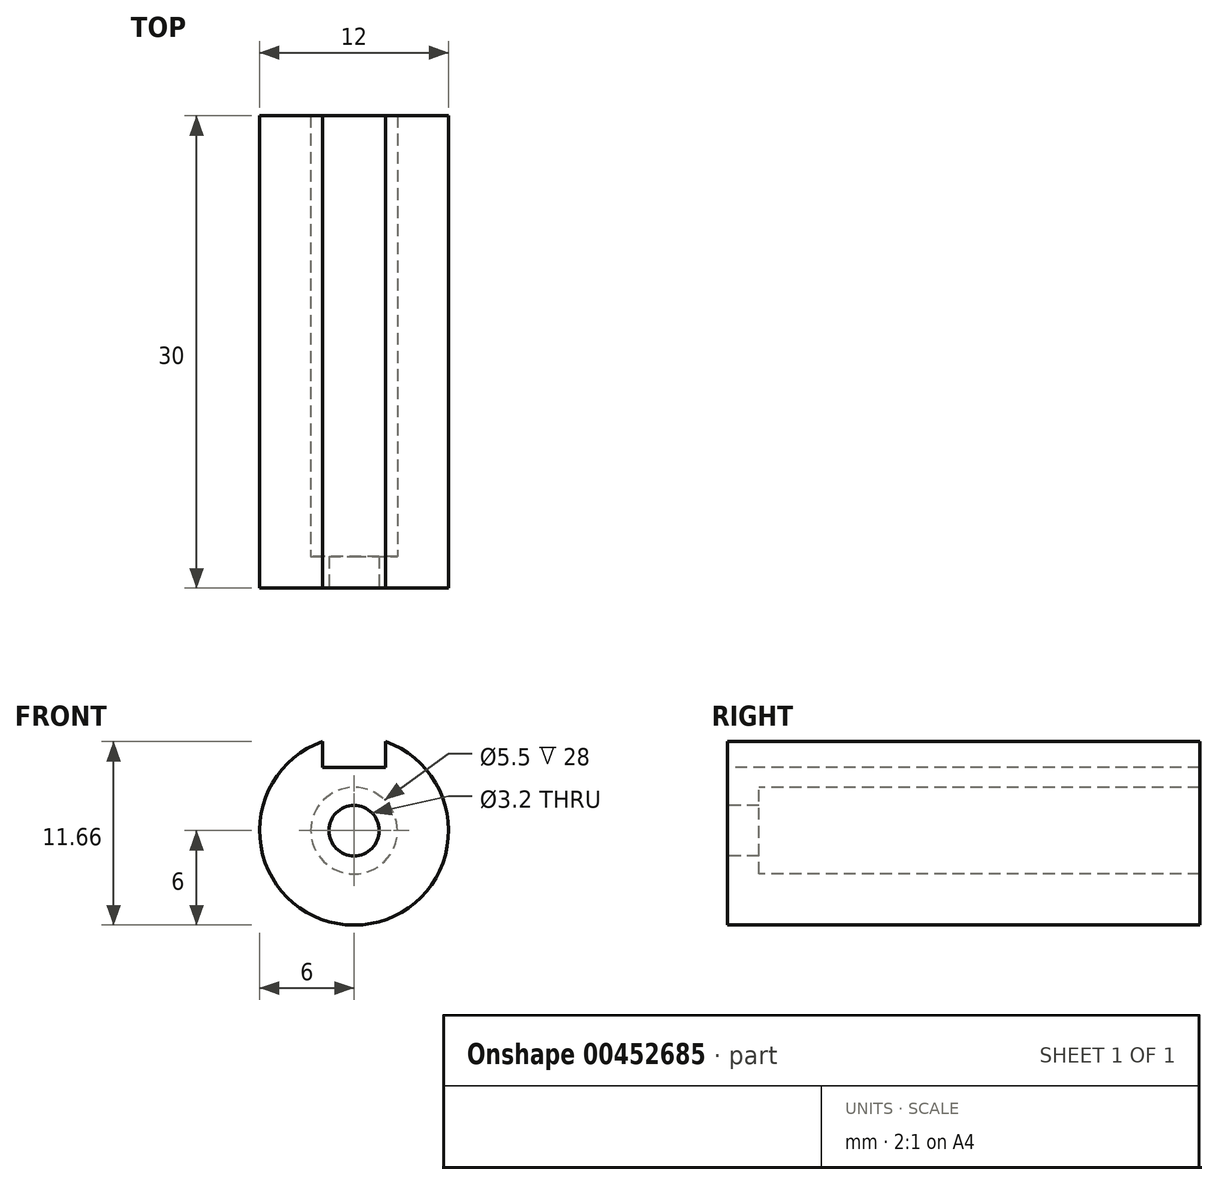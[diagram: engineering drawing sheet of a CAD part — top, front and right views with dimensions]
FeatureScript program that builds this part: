
annotation { "Feature Type Name" : "Feature", "Feature Type Description" : "" }
export const myFeature = defineFeature(function(context is Context, id is Id, definition is map)
    precondition{}
    {
        {
            var Q0;
            Q0=qCreatedBy(makeId("Front.planeOp"),FACE);
            var sketch = newSketch(context, id + "F0", { "sketchPlane" : qUnion([Q0])});
            skCircle(sketch, "E0", {"center": v(0, 0) * mm, "radius": 6 * mm});
            skSolve(sketch);
        }
        {
            var Q0;
            Q0=makeQuery(id+"F0.imprint","IMPRINT",FACE,{"disambiguationData":[TD([[makeQuery(id+"F0.imprint","IMPRINT",EDGE,{"derivedFrom":sQuery(id+"F0.wireOp",EDGE,"E0")}),1.0]])]});
            extrude(context, id + "F1", {"entities" : qUnion([Q0]), "depth" : 30 * mm});
        }
        {
            var Q0;
            Q0=makeQuery(id+"F1.opExtrude","CAP_FACE",FACE,{"disambiguationData":[OSD([sQuery(id+"F0.wireOp",EDGE,"E0")])],"isStart":false});
            var sketch = newSketch(context, id + "F2", { "sketchPlane" : qUnion([Q0])});
            skCircle(sketch, "E1", {"center": v(0, 0) * mm, "radius": 2.75 * mm});
            skSolve(sketch);
        }
        {
            var Q0;
            Q0=qSketchRegion(id+"F2",true);
            extrude(context, id + "F3", {"entities" : qUnion([Q0]), "operationType" : NewBodyOperationType.REMOVE, "endBound" : BoundingType.THROUGH_ALL, "oppositeDirection" : true, "depth" : 25 * mm});
        }
        {
            var Q0;
            Q0=qCreatedBy(makeId("Top.planeOp"),FACE);
            cPlane(context, id + "F4", {"entities" : qUnion([Q0]), "cplaneType" : CPlaneType.OFFSET, "offset" : 4 * mm, "width" : 150 * mm, "height" : 150 * mm});
        }
        {
            var Q0;
            Q0=qCreatedBy(id+"F4.planeOp",FACE);
            var Q1;
            Q1=makeQuery(id+"F1.opExtrude","CAP_EDGE",EDGE,{"disambiguationData":[OSD([sQuery(id+"F0.wireOp",EDGE,"E0")])],"isStart":false});
            cPlane(context, id + "F5", {"entities" : qUnion([Q0, Q1]), "cplaneType" : CPlaneType.LINE_ANGLE, "offset" : 25 * mm, "angle" : 45 * degree, "width" : 150 * mm, "height" : 150 * mm});
        }
        {
            var Q0;
            Q0=qCreatedBy(id+"F5.planeOp",FACE);
            cPlane(context, id + "F6", {"entities" : qUnion([Q0]), "cplaneType" : CPlaneType.OFFSET, "offset" : 3.5 * mm, "width" : 150 * mm, "height" : 150 * mm});
        }
        {
            var Q0;
            Q0=qCreatedBy(id+"F5.planeOp",FACE);
            var Q1;
            Q1=makeQuery(id+"F1.opExtrude","CAP_EDGE",EDGE,{"disambiguationData":[OSD([sQuery(id+"F0.wireOp",EDGE,"E0")])],"isStart":false});
            cPlane(context, id + "F7", {"entities" : qUnion([Q0, Q1]), "cplaneType" : CPlaneType.LINE_ANGLE, "offset" : 25 * mm, "angle" : 90 * degree, "width" : 150 * mm, "height" : 150 * mm});
        }
        {
            var Q0;
            Q0=makeQuery(id+"F1.opExtrude","CAP_FACE",FACE,{"disambiguationData":[OSD([sQuery(id+"F0.wireOp",EDGE,"E0")])],"isStart":false});
            var sketch = newSketch(context, id + "F8", { "sketchPlane" : qUnion([Q0])});
            skCircle(sketch, "E2", {"center": v(0, 0) * mm, "radius": 1.6 * mm});
            skCircle(sketch, "E3", {"center": v(0, 0) * mm, "radius": 5 * mm});
            skSolve(sketch);
        }
        {
            var Q0;
            Q0=qSketchRegion(id+"F8",true);
            extrude(context, id + "F9", {"entities" : qUnion([Q0]), "operationType" : NewBodyOperationType.ADD, "oppositeDirection" : true, "depth" : 2 * mm});
        }
        {
            var Q0;
            Q0=qCreatedBy(makeId("Right.planeOp"),FACE);
            cPlane(context, id + "F10", {"entities" : qUnion([Q0]), "cplaneType" : CPlaneType.OFFSET, "offset" : 6 * mm, "oppositeDirection" : true, "width" : 150 * mm, "height" : 150 * mm});
        }
        {
            var Q0;
            Q0=qCreatedBy(id+"F10.planeOp",FACE);
            var sketch = newSketch(context, id + "F11", { "sketchPlane" : qUnion([Q0])});
            skLineSegment(sketch, "E4.bottom", {"start": v(0, 2) * mm, "end": v(-30, 2) * mm});
            skLineSegment(sketch, "E4.top", {"start": v(0, -2) * mm, "end": v(-30, -2) * mm});
            skLineSegment(sketch, "E4.left", {"start": v(0, 2) * mm, "end": v(0, -2) * mm});
            skLineSegment(sketch, "E4.right", {"start": v(-30, 2) * mm, "end": v(-30, -2) * mm});
            skLineSegment(sketch, "E5", {"start": v(0, 0) * mm, "end": v(-30, 0) * mm, "construction": true});
            skPoint(sketch, "E5.startSnap0", {"position": v(0, 0) * mm});
            skSolve(sketch);
        }
        {
            var Q0;
            Q0=qCreatedBy(id+"F4.planeOp",FACE);
            var sketch = newSketch(context, id + "F12", { "sketchPlane" : qUnion([Q0])});
            skLineSegment(sketch, "E6.bottom", {"start": v(-2, 0) * mm, "end": v(2, 0) * mm});
            skLineSegment(sketch, "E6.top", {"start": v(-2, -30) * mm, "end": v(2, -30) * mm});
            skLineSegment(sketch, "E6.left", {"start": v(-2, 0) * mm, "end": v(-2, -30) * mm});
            skLineSegment(sketch, "E6.right", {"start": v(2, 0) * mm, "end": v(2, -30) * mm});
            skLineSegment(sketch, "E7", {"start": v(0, 0) * mm, "end": v(0, -30) * mm, "construction": true});
            skSolve(sketch);
        }
        {
            var Q0;
            Q0=qSketchRegion(id+"F12",true);
            extrude(context, id + "F13", {"entities" : qUnion([Q0]), "operationType" : NewBodyOperationType.REMOVE, "depth" : 3 * mm});
        }
    });
